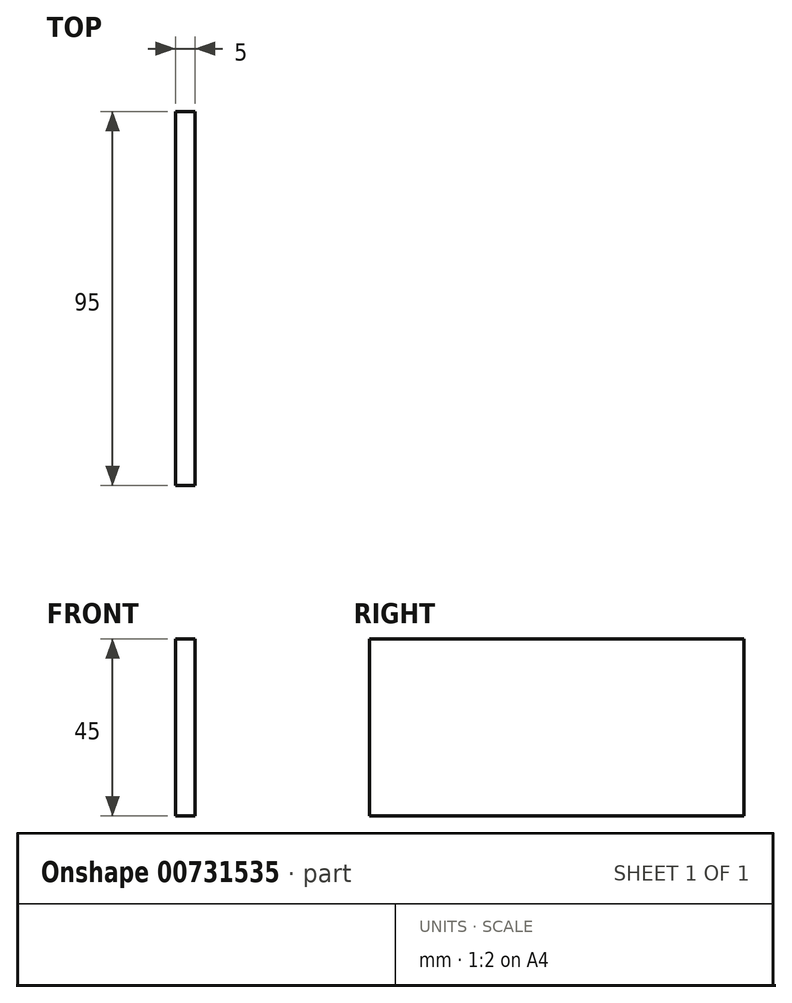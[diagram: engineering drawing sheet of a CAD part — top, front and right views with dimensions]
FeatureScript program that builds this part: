
annotation { "Feature Type Name" : "Feature", "Feature Type Description" : "" }
export const myFeature = defineFeature(function(context is Context, id is Id, definition is map)
    precondition{}
    {
        {
            var Q0;
            Q0=qCreatedBy(makeId("Right.planeOp"),FACE);
            var sketch = newSketch(context, id + "F0", { "sketchPlane" : qUnion([Q0])});
            skLineSegment(sketch, "E0.bottom", {"start": v(0, 0) * mm, "end": v(95, 0) * mm});
            skLineSegment(sketch, "E0.top", {"start": v(0, 45) * mm, "end": v(95, 45) * mm});
            skLineSegment(sketch, "E0.left", {"start": v(0, 0) * mm, "end": v(0, 45) * mm});
            skLineSegment(sketch, "E0.right", {"start": v(95, 0) * mm, "end": v(95, 45) * mm});
            skSolve(sketch);
        }
        {
            var Q0;
            Q0 = qSketchRegion(id + "F0", true);
            extrude(context, id + "F1", {"entities" : qUnion([Q0]), "depth" : 5 * mm, "offsetDistance" : 25 * mm});
        }
    });
